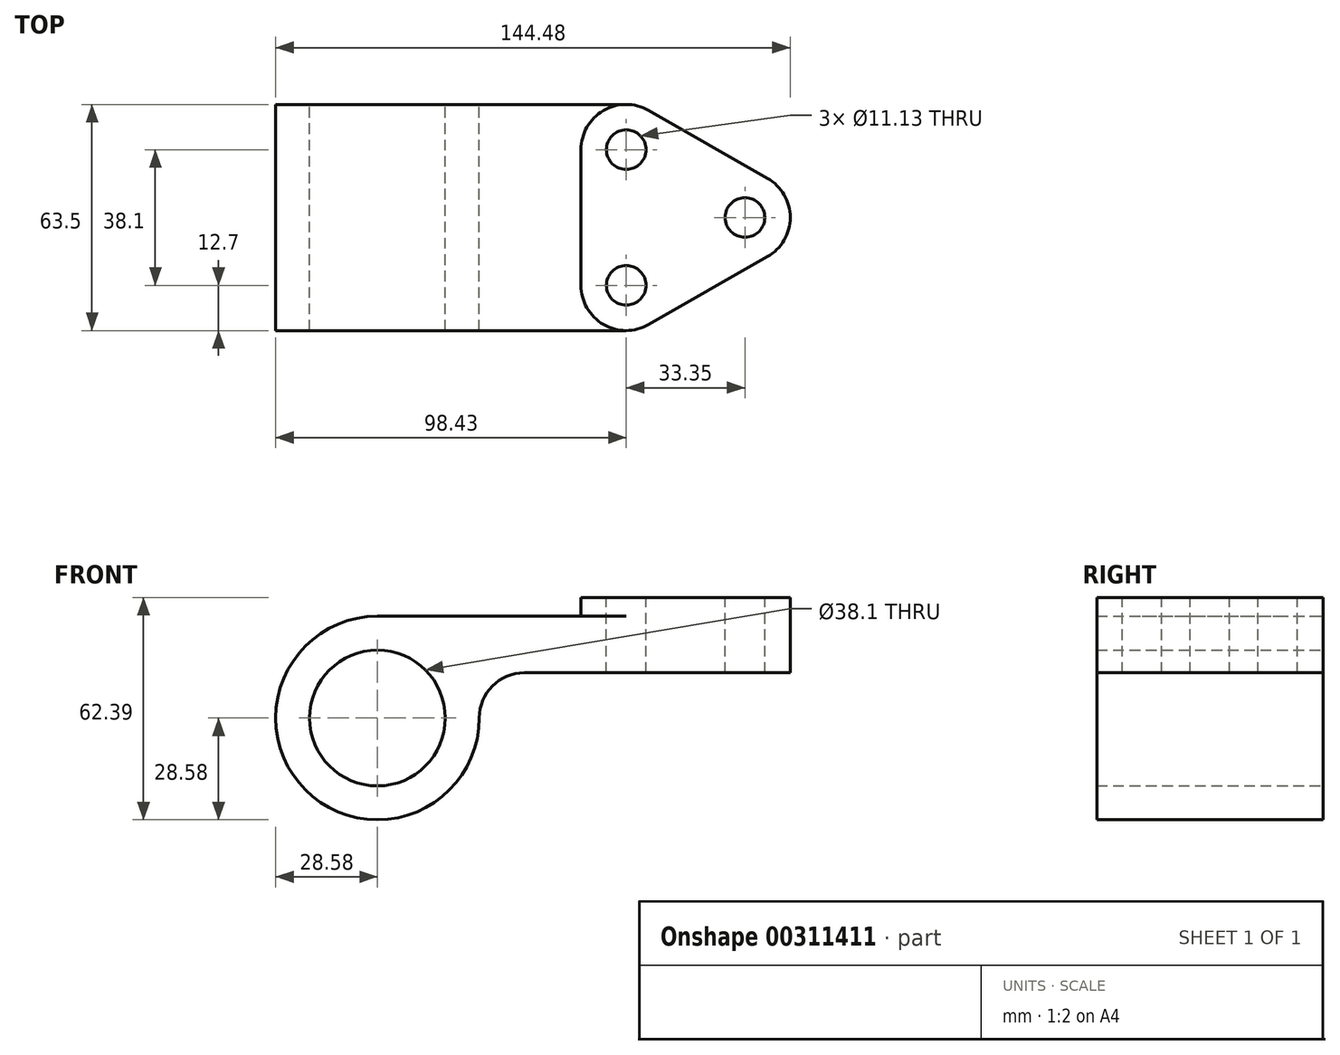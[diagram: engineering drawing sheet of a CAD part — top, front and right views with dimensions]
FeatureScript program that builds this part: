
annotation { "Feature Type Name" : "Feature", "Feature Type Description" : "" }
export const myFeature = defineFeature(function(context is Context, id is Id, definition is map)
    precondition{}
    {
        {
            var Q0;
            Q0=qCreatedBy(makeId("Front.planeOp"),FACE);
            var sketch = newSketch(context, id + "F0", { "sketchPlane" : qUnion([Q0])});
            skCircle(sketch, "E0", {"center": v(0, 0) * mm, "radius": 19.05 * mm});
            skArc(sketch, "E1", {"start": v(0, 28.58) * mm, "mid": v(-20.2, -20.2) * mm, "end": v(28.58, 0) * mm});
            skArc(sketch, "E2", {"start": v(28.57, 0) * mm, "mid": v(32.3, 8.98) * mm, "end": v(41.28, 12.7) * mm});
            skLineSegment(sketch, "E3", {"start": v(41.28, 12.7) * mm, "end": v(69.85, 12.7) * mm});
            skLineSegment(sketch, "E4", {"start": v(69.85, 28.58) * mm, "end": v(69.85, 12.7) * mm});
            skLineSegment(sketch, "E5", {"start": v(69.85, 28.58) * mm, "end": v(0, 28.58) * mm});
            skSolve(sketch);
        }
        {
            var Q0;
            Q0 = qSketchRegion(id + "F0", true);
            extrude(context, id + "F1", {"entities" : qUnion([Q0]), "endBound" : BoundingType.SYMMETRIC, "depth" : 63.5 * mm});
        }
        {
            var Q0;
            Q0=makeQuery(id+"F1.opExtrude","SWEPT_FACE",FACE,{"disambiguationData":[OSD([sQuery(id+"F0.wireOp",EDGE,"E3")])]});
            var sketch = newSketch(context, id + "F2", { "sketchPlane" : qUnion([Q0])});
            skLineSegment(sketch, "E6", {"start": v(57.15, 19.05) * mm, "end": v(57.15, -19.05) * mm});
            skLineSegment(sketch, "E7", {"start": v(76.15, 30.08) * mm, "end": v(109.5, 11.03) * mm});
            skLineSegment(sketch, "E8", {"start": v(76.15, -30.08) * mm, "end": v(109.5, -11.03) * mm});
            skArc(sketch, "E9", {"start": v(57.15, 19.05) * mm, "mid": v(63.47, 30.03) * mm, "end": v(76.15, 30.08) * mm});
            skArc(sketch, "E10", {"start": v(109.5, 11.03) * mm, "mid": v(115.9, 0) * mm, "end": v(109.5, -11.03) * mm});
            skArc(sketch, "E11", {"start": v(76.15, -30.08) * mm, "mid": v(63.47, -30.03) * mm, "end": v(57.15, -19.05) * mm});
            skSolve(sketch);
        }
        {
            var Q0;
            Q0 = qSketchRegion(id + "F2", true);
            extrude(context, id + "F3", {"entities" : qUnion([Q0]), "operationType" : NewBodyOperationType.ADD, "oppositeDirection" : true, "depth" : 21.1 * mm});
        }
        {
            var Q0;
            Q0=makeQuery(id+"F3.opExtrude","CAP_FACE",FACE,{"disambiguationData":[OSD([sQuery(id+"F2.wireOp",EDGE,"E6"),sQuery(id+"F2.wireOp",EDGE,"E7"),sQuery(id+"F2.wireOp",EDGE,"E8"),sQuery(id+"F2.wireOp",EDGE,"E9"),sQuery(id+"F2.wireOp",EDGE,"E10"),sQuery(id+"F2.wireOp",EDGE,"E11")])],"isStart":false});
            var sketch = newSketch(context, id + "F4", { "sketchPlane" : qUnion([Q0])});
            skCircle(sketch, "E12", {"center": v(69.85, 19.05) * mm, "radius": 5.56 * mm});
            skCircle(sketch, "E13", {"center": v(103.2, 0) * mm, "radius": 5.56 * mm});
            skCircle(sketch, "E14", {"center": v(69.85, -19.05) * mm, "radius": 5.56 * mm});
            skArc(sketch, "E15.0", {"start": v(109.5, -11.03) * mm, "mid": v(115.9, 0) * mm, "end": v(109.5, 11.03) * mm});
            skArc(sketch, "E16.0", {"start": v(57.15, -19.05) * mm, "mid": v(63.47, -30.03) * mm, "end": v(76.15, -30.08) * mm});
            skArc(sketch, "E17.0", {"start": v(76.15, 30.08) * mm, "mid": v(63.47, 30.03) * mm, "end": v(57.15, 19.05) * mm});
            skSolve(sketch);
        }
        {
            var Q0;
            Q0=makeQuery(id+"F4.imprint","IMPRINT",FACE,{"disambiguationData":[TD([[makeQuery(id+"F4.imprint","IMPRINT",EDGE,{"derivedFrom":sQuery(id+"F4.wireOp",EDGE,"E13")}),1.0]])]});
            var Q1;
            Q1=makeQuery(id+"F4.imprint","IMPRINT",FACE,{"disambiguationData":[TD([[makeQuery(id+"F4.imprint","IMPRINT",EDGE,{"derivedFrom":sQuery(id+"F4.wireOp",EDGE,"E14")}),1.0]])]});
            var Q2;
            Q2=makeQuery(id+"F4.imprint","IMPRINT",FACE,{"disambiguationData":[TD([[makeQuery(id+"F4.imprint","IMPRINT",EDGE,{"derivedFrom":sQuery(id+"F4.wireOp",EDGE,"E12")}),1.0]])]});
            extrude(context, id + "F5", {"entities" : qUnion([Q0, Q1, Q2]), "operationType" : NewBodyOperationType.REMOVE, "endBound" : BoundingType.THROUGH_ALL, "oppositeDirection" : true, "depth" : 25.4 * mm});
        }
    });
